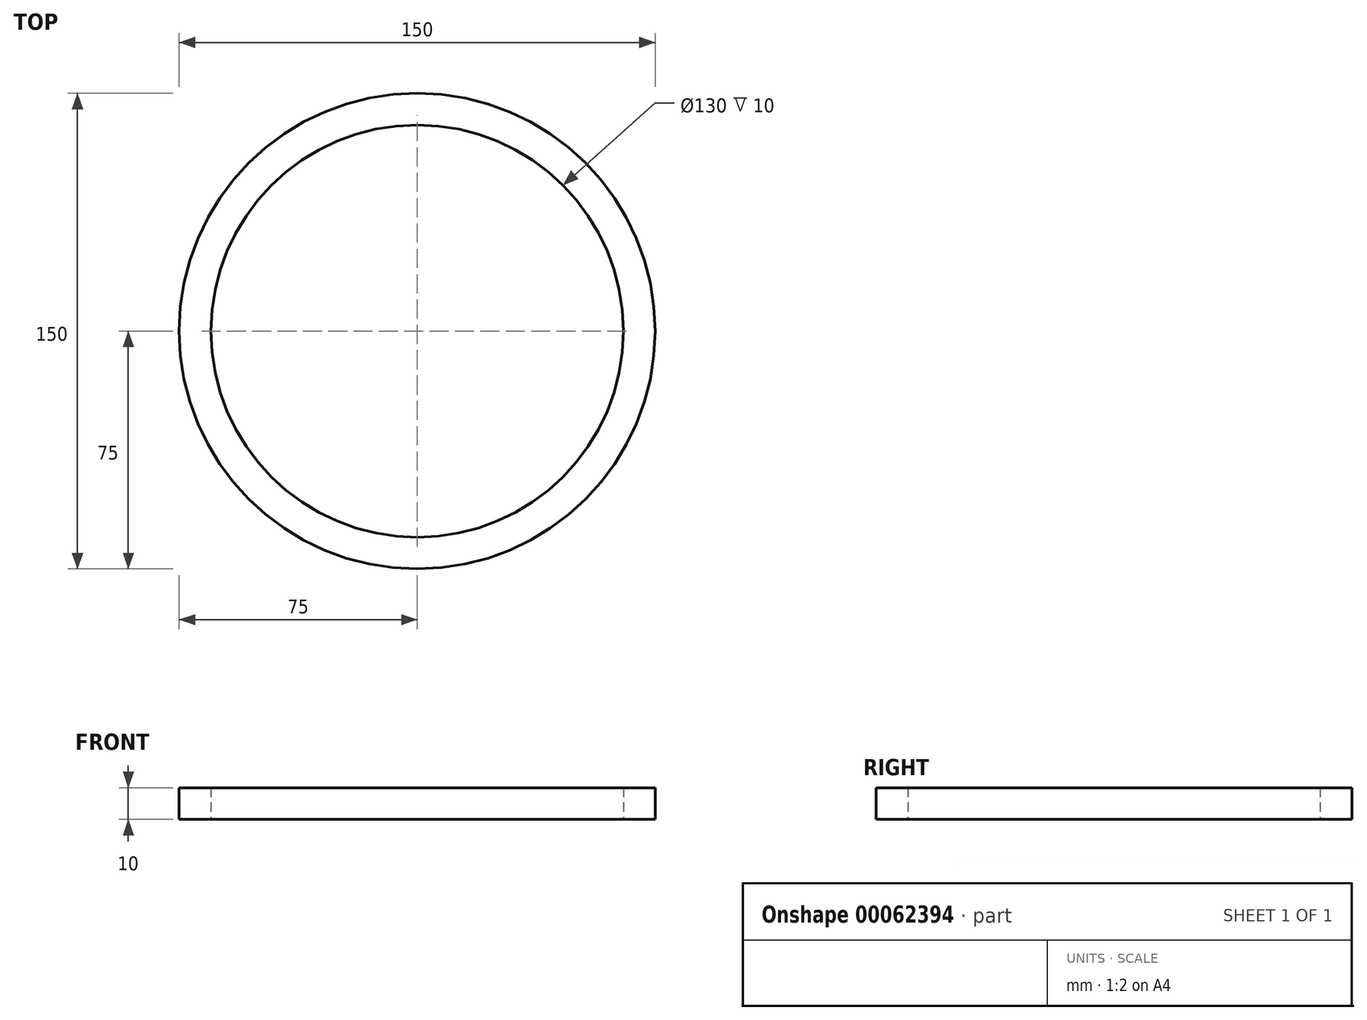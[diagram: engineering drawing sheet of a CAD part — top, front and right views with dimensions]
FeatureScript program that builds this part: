
annotation { "Feature Type Name" : "Feature", "Feature Type Description" : "" }
export const myFeature = defineFeature(function(context is Context, id is Id, definition is map)
    precondition{}
    {
        {
            var Q0;
            Q0=qCreatedBy(makeId("Top.planeOp"),FACE);
            var sketch = newSketch(context, id + "F0", { "sketchPlane" : qUnion([Q0])});
            skCircle(sketch, "E0", {"center": v(0, 0) * mm, "radius": 75 * mm});
            skCircle(sketch, "E1", {"center": v(0, 0) * mm, "radius": 65 * mm});
            skSolve(sketch);
        }
        {
            var Q0;
            Q0=makeQuery(id+"F0.imprint","IMPRINT",FACE,{"disambiguationData":[TD([[makeQuery(id+"F0.imprint","IMPRINT",EDGE,{"derivedFrom":sQuery(id+"F0.wireOp",EDGE,"E0")}),1.0]])]});
            extrude(context, id + "F1", {"entities" : qUnion([Q0]), "depth" : 10 * mm});
        }
    });
